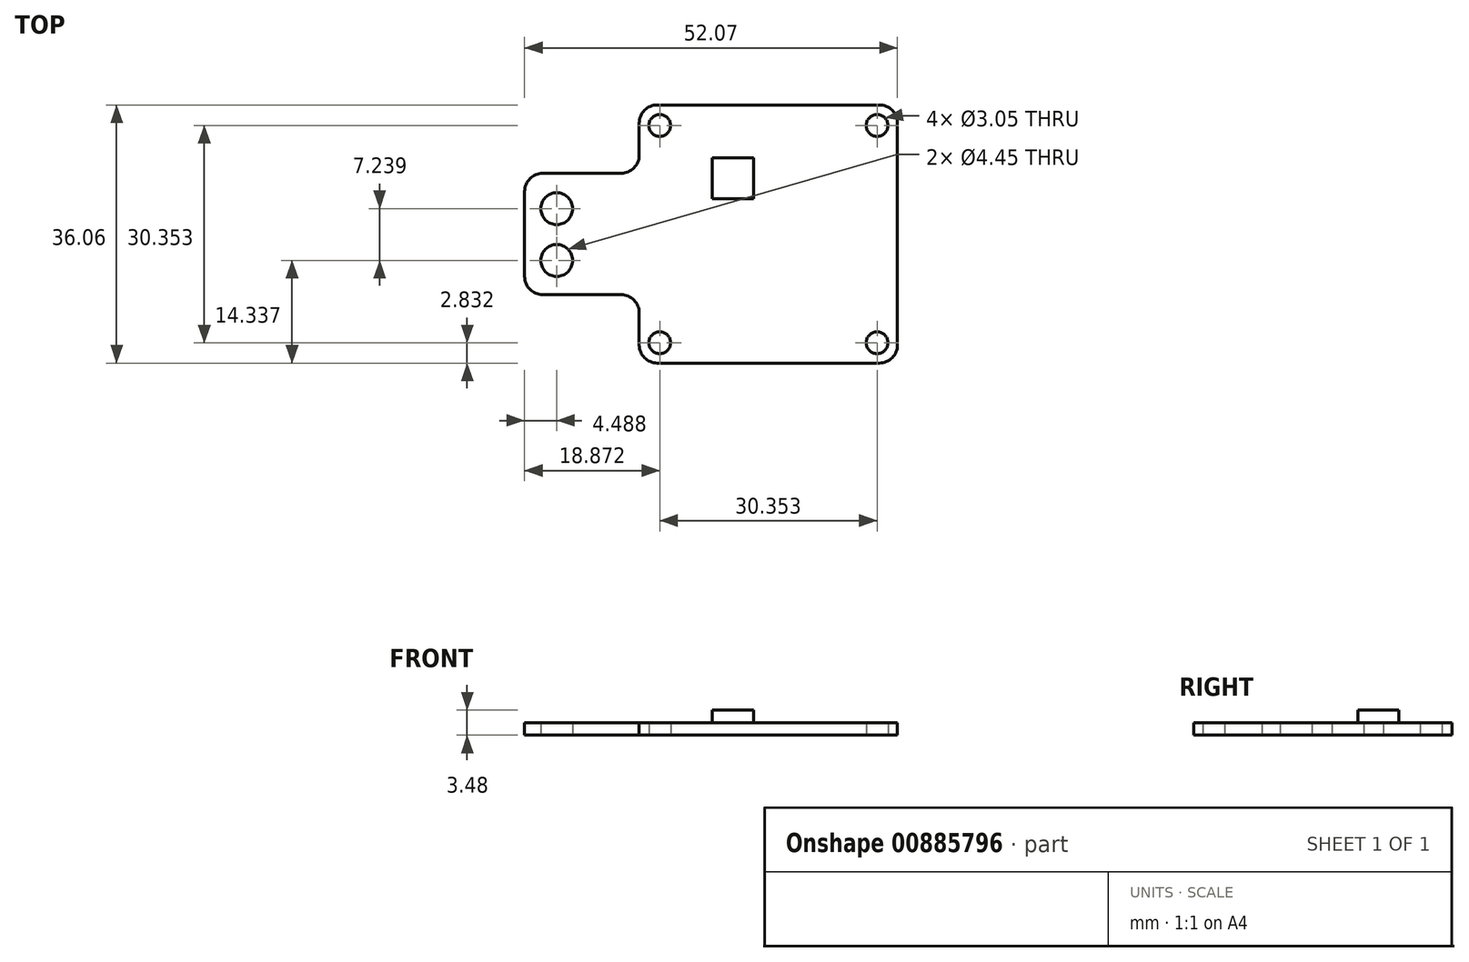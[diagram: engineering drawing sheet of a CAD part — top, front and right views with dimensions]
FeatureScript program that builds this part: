
annotation { "Feature Type Name" : "Feature", "Feature Type Description" : "" }
export const myFeature = defineFeature(function(context is Context, id is Id, definition is map)
    precondition{}
    {
        {
            var Q0;
            Q0=qCreatedBy(makeId("Top.planeOp"),FACE);
            var sketch = newSketch(context, id + "F0", { "sketchPlane" : qUnion([Q0])});
            skLineSegment(sketch, "E0.bottom", {"start": v(18.03, -18.03) * mm, "end": v(-18.03, -18.03) * mm});
            skLineSegment(sketch, "E0.top", {"start": v(18.03, 18.03) * mm, "end": v(-18.03, 18.03) * mm});
            skLineSegment(sketch, "E0.left", {"start": v(18.03, -18.03) * mm, "end": v(18.03, 18.03) * mm});
            skLineSegment(sketch, "E0.right", {"start": v(-18.03, -18.03) * mm, "end": v(-18.03, 18.03) * mm});
            skPoint(sketch, "E0.middle", {"position": v(0, 0) * mm});
            skLineSegment(sketch, "E1.bottom", {"start": v(-34.04, 8.48) * mm, "end": v(18.03, 8.48) * mm});
            skLineSegment(sketch, "E1.top", {"start": v(-34.04, -8.48) * mm, "end": v(18.03, -8.48) * mm});
            skLineSegment(sketch, "E1.left", {"start": v(-34.04, 8.48) * mm, "end": v(-34.04, -8.48) * mm});
            skLineSegment(sketch, "E1.right", {"start": v(18.03, 8.48) * mm, "end": v(18.03, -8.48) * mm});
            skCircle(sketch, "E2", {"center": v(-15.17, 15.16) * mm, "radius": 1.52 * mm});
            skCircle(sketch, "E3", {"center": v(15.19, 15.16) * mm, "radius": 1.52 * mm});
            skCircle(sketch, "E4", {"center": v(-15.17, -15.2) * mm, "radius": 1.52 * mm});
            skCircle(sketch, "E5", {"center": v(15.19, -15.2) * mm, "radius": 1.52 * mm});
            skCircle(sketch, "E6", {"center": v(-29.55, -3.7) * mm, "radius": 2.22 * mm});
            skCircle(sketch, "E7", {"center": v(-29.55, 3.55) * mm, "radius": 2.22 * mm});
            skSolve(sketch);
        }
        {
            var Q0;
            Q0 = qSketchRegion(id + "F0", true);
            extrude(context, id + "F1", {"entities" : qUnion([Q0]), "depth" : 1.7 * mm, "offsetDistance" : 25.4 * mm});
        }
        {
            var Q0;
            Q0=makeQuery(id+"F1.opExtrude","SWEPT_EDGE",EDGE,{"disambiguationData":[OSD([sQuery(id+"F0.wireOp",EDGE,"E0.top"),sQuery(id+"F0.wireOp",EDGE,"E0.right")])]});
            var Q1;
            Q1=makeQuery(id+"F1.opExtrude","SWEPT_EDGE",EDGE,{"disambiguationData":[OSD([sQuery(id+"F0.wireOp",EDGE,"E0.bottom"),sQuery(id+"F0.wireOp",EDGE,"E0.right")])]});
            var Q2;
            Q2=makeQuery(id+"F1.opExtrude","SWEPT_EDGE",EDGE,{"disambiguationData":[OSD([sQuery(id+"F0.wireOp",EDGE,"E0.bottom"),sQuery(id+"F0.wireOp",EDGE,"E0.left")])]});
            var Q3;
            Q3=makeQuery(id+"F1.opExtrude","SWEPT_EDGE",EDGE,{"disambiguationData":[OSD([sQuery(id+"F0.wireOp",EDGE,"E0.top"),sQuery(id+"F0.wireOp",EDGE,"E0.left")])]});
            fillet(context, id + "F2", {"entities" : qUnion([Q0, Q1, Q2, Q3]), "radius" : 2.54 * mm, "tangentPropagation" : true, "allowEdgeOverflow" : false});
        }
        {
            var Q0;
            Q0=makeQuery(id+"F1.opExtrude","SWEPT_EDGE",EDGE,{"disambiguationData":[OSD([sQuery(id+"F0.wireOp",EDGE,"E0.right"),sQuery(id+"F0.wireOp",EDGE,"E1.bottom")])]});
            var Q1;
            Q1=makeQuery(id+"F1.opExtrude","SWEPT_EDGE",EDGE,{"disambiguationData":[OSD([sQuery(id+"F0.wireOp",EDGE,"E0.right"),sQuery(id+"F0.wireOp",EDGE,"E1.top")])]});
            var Q2;
            Q2=makeQuery(id+"F1.opExtrude","SWEPT_EDGE",EDGE,{"disambiguationData":[OSD([sQuery(id+"F0.wireOp",EDGE,"E1.top"),sQuery(id+"F0.wireOp",EDGE,"E1.left")])]});
            var Q3;
            Q3=makeQuery(id+"F1.opExtrude","SWEPT_EDGE",EDGE,{"disambiguationData":[OSD([sQuery(id+"F0.wireOp",EDGE,"E1.bottom"),sQuery(id+"F0.wireOp",EDGE,"E1.left")])]});
            fillet(context, id + "F3", {"entities" : qUnion([Q0, Q1, Q2, Q3]), "radius" : 2.54 * mm, "tangentPropagation" : true, "allowEdgeOverflow" : false});
        }
        {
            var Q0;
            Q0=makeQuery(id+"F1.opExtrude","CAP_FACE",FACE,{"disambiguationData":[OSD([sQuery(id+"F0.wireOp",EDGE,"E0.bottom"),sQuery(id+"F0.wireOp",EDGE,"E0.top"),sQuery(id+"F0.wireOp",EDGE,"E0.left"),sQuery(id+"F0.wireOp",EDGE,"E0.right"),sQuery(id+"F0.wireOp",EDGE,"E1.bottom"),sQuery(id+"F0.wireOp",EDGE,"E1.top"),sQuery(id+"F0.wireOp",EDGE,"E1.left"),sQuery(id+"F0.wireOp",EDGE,"E1.right"),sQuery(id+"F0.wireOp",EDGE,"E2"),sQuery(id+"F0.wireOp",EDGE,"E3"),sQuery(id+"F0.wireOp",EDGE,"E4"),sQuery(id+"F0.wireOp",EDGE,"E5"),sQuery(id+"F0.wireOp",EDGE,"E6"),sQuery(id+"F0.wireOp",EDGE,"E7")])],"isStart":false});
            var sketch = newSketch(context, id + "F4", { "sketchPlane" : qUnion([Q0])});
            skLineSegment(sketch, "E8.bottom", {"start": v(-7.82, 10.62) * mm, "end": v(-2.05, 10.62) * mm});
            skLineSegment(sketch, "E8.top", {"start": v(-7.82, 4.92) * mm, "end": v(-2.05, 4.92) * mm});
            skLineSegment(sketch, "E8.left", {"start": v(-7.82, 10.62) * mm, "end": v(-7.82, 4.92) * mm});
            skLineSegment(sketch, "E8.right", {"start": v(-2.05, 10.62) * mm, "end": v(-2.05, 4.92) * mm});
            skSolve(sketch);
        }
        {
            var Q0;
            Q0 = qSketchRegion(id + "F4", true);
            extrude(context, id + "F5", {"entities" : qUnion([Q0]), "operationType" : NewBodyOperationType.ADD, "depth" : 1.78 * mm, "offsetDistance" : 25.4 * mm});
        }
    });
